# Revit family: Bath_Mixer-GROHE-ATRIO-32653_Series-copy
name_source: partatom
category: Plumbing Fixtures
revit_build: Autodesk Revit 2014 (Build: 20130308_1515(x64)
units: mm (PartAtom-declared; Revit-internal decimal feet)

## types (1)
- 32653003
    Assembly Code = D2020300
    CW Connection = Yes
    CWFU = 3
    Cold Water Connection Diameter = 13 mm
    Default Elevation = 0 mm  [stored 0 ft]
    Description = ATRIO Single-lever Bathtub Faucet, Floor Mounted
    Finish = Metal-Grohe-000-Starlight Chrome
    Flow Rate = Hand shower Sena Stick (26 465), 1.75gpm
    HW Connection = Yes
    HWFU = 3
    Height = 936 mm  [stored 3.07087 ft]
    Hose Height = 643 mm  [stored 2.10958 ft]
    Hot Water Connection Diameter = 1"
    Installation Type = Surface Mounted
    Length = 276 mm
    Manufacturer = GROHE
    Material = Metal-Grohe-000-Starlight Chrome
    Model = 32653003
    Price = Prices may vary. Please consult Manufacturer Representative for most up-to-date price list.
    Product Page URL = https://www.grohe.ca
    Tempered Water Connection Diameter = 13 mm
    URL = https://www.grohe.us
    Vent Connection = No
    WFU = 4
    Warranty Documentation Link = https://www.grohe.ca
    Waste Connection = No
    Width = 240 mm  [stored 0.787402 ft]

note: [stored X ft] marks values corroborated as IEEE doubles in the binary element streams (Revit-internal decimal feet)

## geometry (parser evidence)
native form markers: Sweep x1
no freeform markers — native parametric forms only
